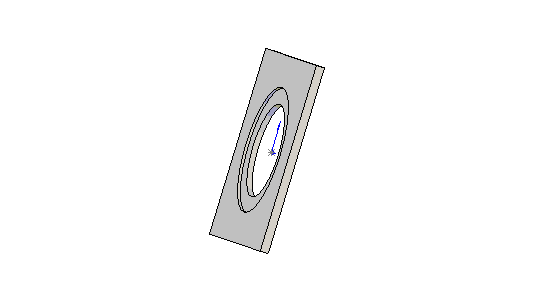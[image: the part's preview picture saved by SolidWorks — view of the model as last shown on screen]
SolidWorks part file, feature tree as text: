
SOLIDWORKS PART (.sldprt)
format: sldprt  version: not decoded by parser v0  size: 81,920 bytes
history: native  units: mm
features: sketch x3, cut_extrude x2, extrude x1 (+11 scaffold rows collapsed)
feature tree (17):
  scaffold x11  (default folders/planes/origin — collapsed)
  sketch  "Sketch1"  dims[D1=76.2mm D2=76.2mm D3=38.1mm D4=38.1mm]
  extrude  "Extrude1"  Depth=3.429mm
  sketch  "Sketch2"  dims[D1=51.308mm]
  cut_extrude  "Cut-Extrude1"  Depth=1.143mm
  sketch  "Sketch3"  dims[D1=38.1mm]
  cut_extrude  "Cut-Extrude2"  [1 undecoded]
decode coverage: 5 of 6 modeling features carry decoded parameters
note: 1 parameter value undecoded
note: suppression state not decoded; provenance and decode notes live in map.json
